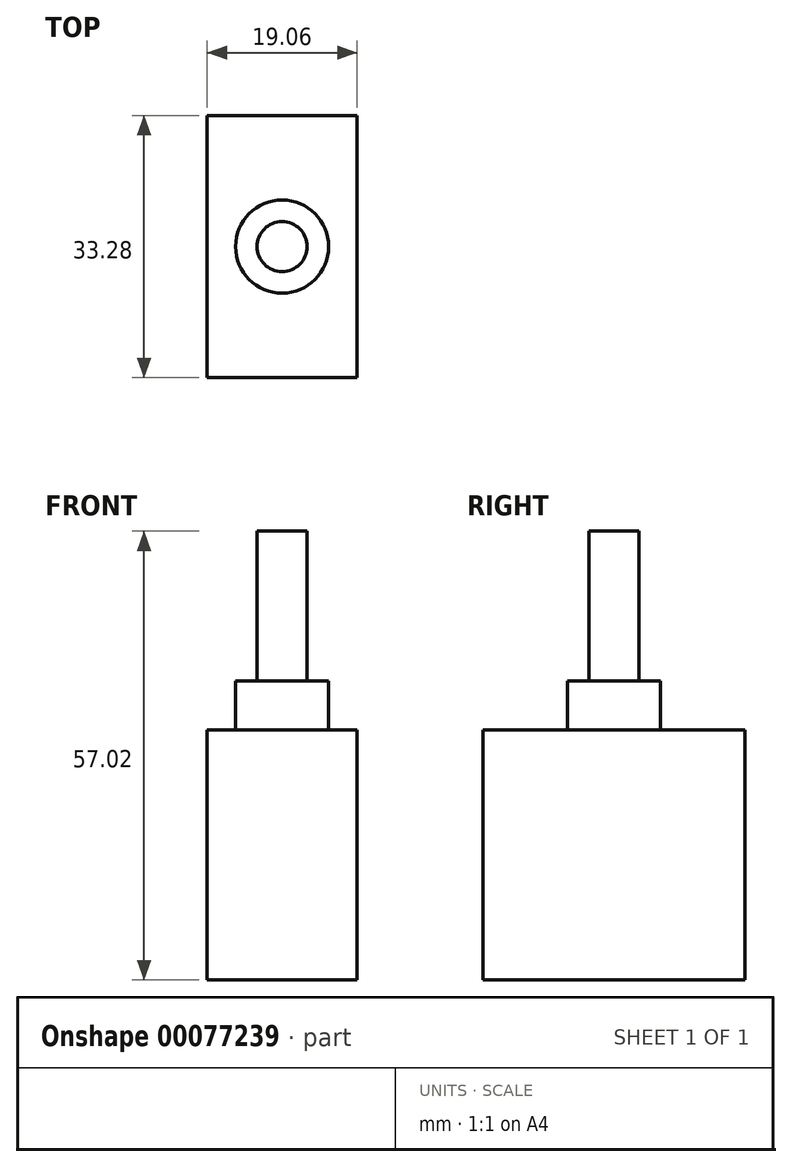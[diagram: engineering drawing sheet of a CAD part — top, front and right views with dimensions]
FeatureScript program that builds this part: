
annotation { "Feature Type Name" : "Feature", "Feature Type Description" : "" }
export const myFeature = defineFeature(function(context is Context, id is Id, definition is map)
    precondition{}
    {
        {
            var Q0;
            Q0=qCreatedBy(makeId("Top.planeOp"),FACE);
            var sketch = newSketch(context, id + "F0", { "sketchPlane" : qUnion([Q0])});
            skCircle(sketch, "E0", {"center": v(0, 0) * mm, "radius": 5.9 * mm});
            skSolve(sketch);
        }
        {
            var Q0;
            Q0 = qSketchRegion(id + "F0", true);
            extrude(context, id + "F1", {"entities" : qUnion([Q0]), "depth" : 6.22 * mm});
        }
        {
            var Q0;
            Q0=makeQuery(id+"F1.opExtrude","CAP_FACE",FACE,{"disambiguationData":[OSD([sQuery(id+"F0.wireOp",EDGE,"E0")])],"isStart":false});
            var sketch = newSketch(context, id + "F2", { "sketchPlane" : qUnion([Q0])});
            skCircle(sketch, "E1", {"center": v(0, 0) * mm, "radius": 3.18 * mm});
            skSolve(sketch);
        }
        {
            var Q0;
            Q0 = qSketchRegion(id + "F2", true);
            extrude(context, id + "F3", {"entities" : qUnion([Q0]), "operationType" : NewBodyOperationType.ADD, "depth" : 19.05 * mm});
        }
        {
            var Q0;
            Q0=makeQuery(id+"F1.opExtrude","CAP_FACE",FACE,{"disambiguationData":[OSD([sQuery(id+"F0.wireOp",EDGE,"E0")])],"isStart":true});
            var sketch = newSketch(context, id + "F4", { "sketchPlane" : qUnion([Q0])});
            skLineSegment(sketch, "E2.bottom", {"start": v(-9.52, 16.64) * mm, "end": v(9.53, 16.64) * mm});
            skLineSegment(sketch, "E2.top", {"start": v(-9.53, -16.64) * mm, "end": v(9.52, -16.64) * mm});
            skLineSegment(sketch, "E2.left", {"start": v(-9.52, 16.64) * mm, "end": v(-9.53, -16.64) * mm});
            skLineSegment(sketch, "E2.right", {"start": v(9.53, 16.64) * mm, "end": v(9.52, -16.64) * mm});
            skLineSegment(sketch, "E3", {"start": v(-9.53, 16.64) * mm, "end": v(9.53, -16.64) * mm});
            skSolve(sketch);
        }
        {
            var Q0;
            Q0 = qSketchRegion(id + "F4", true);
            extrude(context, id + "F5", {"entities" : qUnion([Q0]), "operationType" : NewBodyOperationType.ADD, "depth" : 31.75 * mm});
        }
    });
